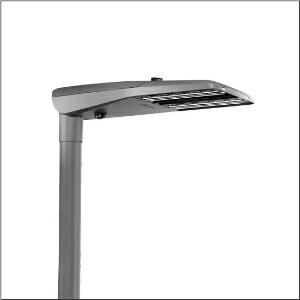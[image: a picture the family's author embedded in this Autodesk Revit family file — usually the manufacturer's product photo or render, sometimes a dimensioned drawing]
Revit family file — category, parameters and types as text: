
# Revit family: streetlight_sl_11_iq_midi___pc-r_5xc3f51y08me_63e7
name_source: partatom
category: Lighting Fixtures
units: mm (PartAtom-declared; Revit-internal decimal feet)

## family parameters
Cut with Voids When Loaded = No
Host = Face
Light Source = No
Part Type = Normal
Room Calculation Point = No
Round Connector Dimension = Use Diameter
Shared = No

## types (1)
- --- (1 x LED, 15540 lm, 122.7 W, 3000K)
    Apparent Load = 123 VA
    CIE Flux Codes = 37 73 96 100 100
    Color Rendering = 70
    Color Temperature = 3000K
    Default Elevation = 1800 mm
    Description = Streetlight SL 11 iQ midi, mast luminaire, primary light control with 3 zone facetted reflector, of plastic, silver coated, highly specular, primary optical cover: cover, of PMMA, transparent, light distribution: PC-R, light emission: direct distribution, primary light characteristic: asymmetric, right, installation type: post-top, side-entry, LED, High Power LED, rated luminous flux: 15.540lm, luminous efficacy: 127lm/W, light colour: 730, colour temperature: 3000K, control: pre-setting: logarithmic dimming characteristic, Street-Remote, Auto-Match, Temp-Guard, Lumen-Switch, Night-Set, Smart-Wire, Light-Fading, Desk-Remote (wireless, voltage-free reading and setting of iQ features in the workshop via application-optimized NFC function/RFID function), optimised constant luminous flux control (CLO 2.0), with cable H07RN-F 5x 1.5mm², mains connection: 230..240V, AC, 50/60Hz, connection cable pre-assembled, cable length: 12,5m, start of lifetime: 123W, end of service life: 130W, reduction: 56W, luminaire housing, of diecast aluminium, powder-coated, Siteco® metallic grey (DB 702S), please order mast flange separately, inclination adjustable without tools: 0°, 5°, 10°, 15° (post-top) | 0°, -5°, -10°, -15° (side-entry), sealing non-destructively replaceable, multi-level sealing system, length: 780mm, width: 376mm, height: 118mm, mast flange for spigot size: 42mm (side-entry): 5XC10008XM4, 60/48mm (side-entry/post-top): 5XC10108XM2, 76/60mm (side-entry/post-top): 5XC10108XM1, equipment: Power, Smart Interface below and above, protection rating (complete): IP66, insulation class (complete): insulation class II (safety insulation), certification: CE, ENEC, VDE, UKCA, impact resistance: IK09, permissible operating ambient temperature for outdoor applications: -25..+50°C, standard-compliant lighting for roads and squares, Environmental Product Declaration (EPD) tested and certified by an independent institute, packaging unit: 1 piece

Light Distribution: PC-R
    Height = 118 mm
    Lamp = 1 x LED
    Lamp Light Flux = 15540 lm
    Lamp Power = 122.7 W
    Lamp count = 1
    Length = 780 mm
    Luminous efficacy = 127 lm/W
    Manufacturer = Siteco
    ModVariant = No
    Model = 5XC3F51Y08ME
    Number of Poles = 1
    OnlyDefault = Yes
    Power Factor = 1
    Product Name = Streetlight SL 11 iQ midi | PC-R
    Product group = mast luminaire | pylon top
    ProductGroupID = 6100
    Protection Class = Protection class II
    Protection Degree = IP 66
    RLX_Detail_Level = 1
    RLX_Emergency_Light_Flux = 0 lm
    RLX_Emergency_Type = 0
    RLX_Emergency_Type_DB = No
    RlxData = <blob elided: 73425 chars, md5=d6ab72d9>
    Socket = socket
    Standby Power = 0 W
    System Light Flux = 15540 lm
    System Power = 123 W
    Type Comments = factory setting: luminous flux: 100 % | dim-lin: 254 | 552 mA
    Type Image = l_1004429.jpg
    URL = http://relux.com
    VarID = @adj_102765
    Voltage = 0 V
    Weight = 0.00 kg
    Width = 376 mm

## geometry (parser evidence)
native form markers: Blend x4, Sweep x9
no freeform markers — native parametric forms only
